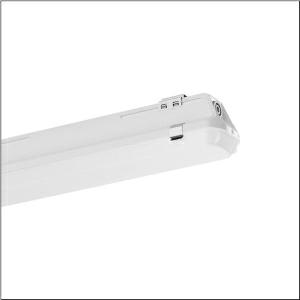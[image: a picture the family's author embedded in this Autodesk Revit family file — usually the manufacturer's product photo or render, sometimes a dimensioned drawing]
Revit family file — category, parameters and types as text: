
# Revit family: monsun_11_51fp108p460h
name_source: partatom
category: Lighting Fixtures
units: mm (PartAtom-declared; Revit-internal decimal feet)

## family parameters
Cut with Voids When Loaded = No
Host = Face
Light Source = No
Part Type = Normal
Room Calculation Point = No
Round Connector Dimension = Use Diameter
Shared = No

## types (1)
- Monsun 11 (1 x LED, 6100 lm, 33.9 W, 4000K)
    Apparent Load = 34 VA
    CIE Flux Codes = 47 77 93 94 100
    Color Rendering = 80
    Color Temperature = 4000K
    Default Elevation = 1800 mm
    Description = Monsun 11, damp-proof luminaire, chain hanger, primary optical cover: enclosure, of PMMA, light emission: direct distribution, primary light characteristic: symmetric, installation type: suspended mounting, surface-mounted, horizontal mounting, vertical mounting, LED, rated luminous flux: 6.100lm, luminous efficacy: 180lm/W, light colour: 840, colour temperature: 4000K, control gear: ON/OFF, with terminal, 3-pole, max. 2.5mm², mains connection: 220..240V, AC, 50/60Hz, rated input power: 34W, luminaire housing, of glass-fibre reinforced polyester, uncoated, bright grey, incl. chain hanger, length: 1.590mm, width: 90mm, height: 88mm, clip for enclosure, of stainless steel (V2A), ceiling mounting element, of stainless steel (V2A), chain hanger, of stainless steel (V2A), protection rating (complete): IP66, insulation class (complete): insulation class I (protective earthing), certification: CE, ENEC, VDE, UKCA, protection symbol: D, impact resistance: IK04, permissible operating ambient temperature: -35..+40°C, standard: EN 50419, EN 60598-2-1, no direct snow, no direct sun, no direct rain, for indoor or canopied outdoor use, corresponds to IFS (International Featured Standards) requirements for safety and quality in the food industry, contact your sales advisor before using the luminaires in applications with unclear chemical exposure, large temperature fluctuations or condensation-forming humidity, LABS conformity tested according to VDMA 24364:2018-05, packaging unit: 1 piece
    Height = 89 mm
    Lamp = 1 x LED
    Lamp Light Flux = 6100 lm
    Lamp Power = 33.9 W
    Lamp count = 1
    Length = 1590 mm
    Luminous efficacy = 180 lm/W
    Manufacturer = Siteco
    ModVariant = No
    Model = 51FP108P460H
    Mounting Place = Ceiling
    Mounting Type = Surface mounted
    Number of Poles = 1
    OnlyDefault = Yes
    Power Factor = 1
    Product Name = Monsun 11
    Product group = damp-proof luminaire
    ProductGroupID = 300
    Protection Class = Protection class I
    Protection Degree = IP 66
    RLX_Detail_Level = 1
    RLX_Emergency_Light_Flux = 0 lm
    RLX_Emergency_Type = 0
    RLX_Emergency_Type_DB = No
    RlxData = <blob elided: 88321 chars, md5=3ecd3550>
    Socket = socket
    Standby Power = 0 W
    System Light Flux = 6100 lm
    System Power = 34 W
    Type Comments = Product without accessories
    Type Image = l_1349237.jpg
    URL = http://relux.com
    VarID = ---
    Voltage = 0 V
    Weight = 0.00 kg
    Width = 90 mm

## geometry (parser evidence)
native form markers: Blend x4, Sweep x13
no freeform markers — native parametric forms only
